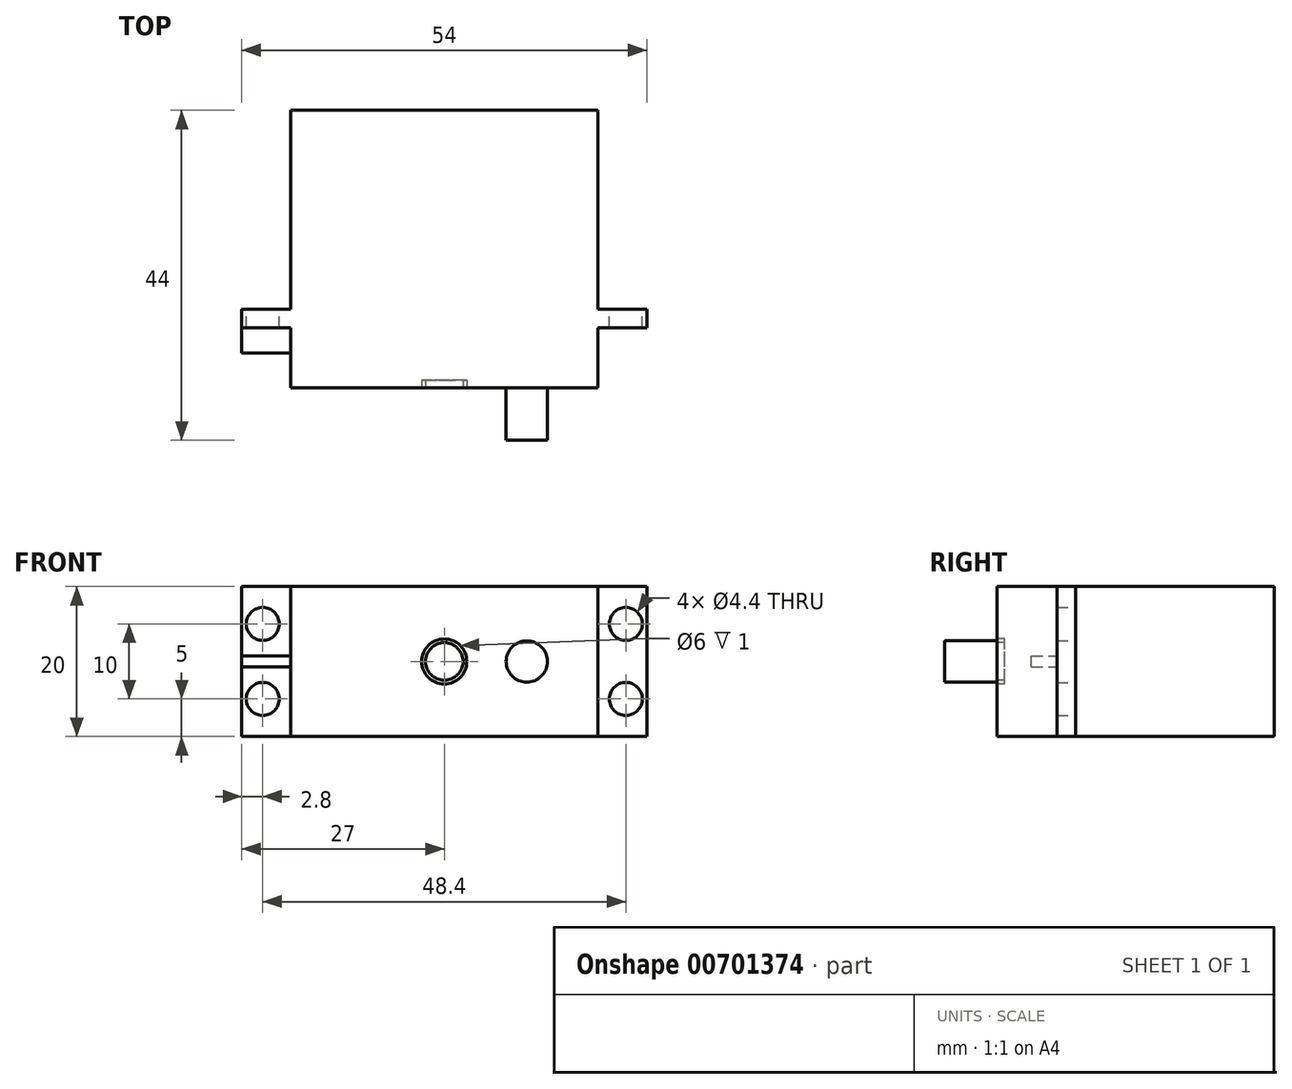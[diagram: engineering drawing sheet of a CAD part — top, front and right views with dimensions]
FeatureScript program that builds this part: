
annotation { "Feature Type Name" : "Feature", "Feature Type Description" : "" }
export const myFeature = defineFeature(function(context is Context, id is Id, definition is map)
    precondition{}
    {
        {
            var Q0;
            Q0=qCreatedBy(makeId("Front.planeOp"),FACE);
            var sketch = newSketch(context, id + "F0", { "sketchPlane" : qUnion([Q0])});
            skLineSegment(sketch, "E0.bottom", {"start": v(20.5, -10) * mm, "end": v(-20.5, -10) * mm});
            skLineSegment(sketch, "E0.top", {"start": v(20.5, 10) * mm, "end": v(-20.5, 10) * mm});
            skLineSegment(sketch, "E0.left", {"start": v(20.5, -10) * mm, "end": v(20.5, 10) * mm});
            skLineSegment(sketch, "E0.right", {"start": v(-20.5, -10) * mm, "end": v(-20.5, 10) * mm});
            skPoint(sketch, "E0.middle", {"position": v(0, 0) * mm});
            skSolve(sketch);
        }
        {
            var Q0;
            Q0=makeQuery(id+"F0.imprint","IMPRINT",FACE,{"disambiguationData":[TD([[makeQuery(id+"F0.imprint","IMPRINT",EDGE,{"derivedFrom":sQuery(id+"F0.wireOp",EDGE,"E0.bottom")}),-1.0]])]});
            extrude(context, id + "F1", {"entities" : qUnion([Q0]), "depth" : 26.5 * mm});
        }
        {
            var Q0;
            Q0=makeQuery(id+"F1.opExtrude","CAP_FACE",FACE,{"disambiguationData":[OSD([sQuery(id+"F0.wireOp",EDGE,"E0.bottom"),sQuery(id+"F0.wireOp",EDGE,"E0.top"),sQuery(id+"F0.wireOp",EDGE,"E0.left"),sQuery(id+"F0.wireOp",EDGE,"E0.right")])],"isStart":false});
            var sketch = newSketch(context, id + "F2", { "sketchPlane" : qUnion([Q0])});
            skLineSegment(sketch, "E1.bottom", {"start": v(27, -10) * mm, "end": v(-27, -10) * mm});
            skLineSegment(sketch, "E1.top", {"start": v(27, 10) * mm, "end": v(-27, 10) * mm});
            skLineSegment(sketch, "E1.left", {"start": v(27, -10) * mm, "end": v(27, 10) * mm});
            skLineSegment(sketch, "E1.right", {"start": v(-27, -10) * mm, "end": v(-27, 10) * mm});
            skPoint(sketch, "E1.middle", {"position": v(0, 0) * mm});
            skCircle(sketch, "E2", {"center": v(24.2, 5) * mm, "radius": 2.2 * mm});
            skCircle(sketch, "E3.MirrorC", {"center": v(24.2, -5) * mm, "radius": 2.2 * mm});
            skCircle(sketch, "E4.MirrorC", {"center": v(-24.2, -5) * mm, "radius": 2.2 * mm});
            skCircle(sketch, "E5.MirrorC", {"center": v(-24.2, 5) * mm, "radius": 2.2 * mm});
            skSolve(sketch);
        }
        {
            var Q0;
            {var subQ0=sQuery(id+"F2.wireOp",EDGE,"E1.right");Q0=makeQuery(id+"F2.imprint","IMPRINT",FACE,{"disambiguationData":[TD([[makeQuery(id+"F2.imprint","IMPRINT",EDGE,{"derivedFrom":subQ0}),-1.0]])]});}
            var Q1;
            {var subQ0=sQuery(id+"F2.wireOp",EDGE,"E1.left");Q1=makeQuery(id+"F2.imprint","IMPRINT",FACE,{"disambiguationData":[TD([[makeQuery(id+"F2.imprint","IMPRINT",EDGE,{"derivedFrom":subQ0}),1.0]])]});}
            var Q2;
            {var subQ1=makeQuery(id+"F1.opExtrude","CAP_EDGE",EDGE,{"disambiguationData":[OSD([sQuery(id+"F0.wireOp",EDGE,"E0.left")])],"isStart":false});Q2=makeQuery(id+"F2.imprint","IMPRINT",FACE,{"disambiguationData":[TD([[makeQuery(id+"F2.imprint","IMPRINT",EDGE,{"derivedFrom":subQ1}),1.0]])]});}
            extrude(context, id + "F3", {"entities" : qUnion([Q0, Q1, Q2]), "operationType" : NewBodyOperationType.ADD, "depth" : 2.5 * mm});
        }
        {
            var Q0;
            Q0=makeQuery(id+"F3.opExtrude","CAP_FACE",FACE,{"disambiguationData":[OSD([sQuery(id+"F2.wireOp",EDGE,"E1.bottom"),sQuery(id+"F2.wireOp",EDGE,"E1.top"),sQuery(id+"F2.wireOp",EDGE,"E1.left"),sQuery(id+"F2.wireOp",EDGE,"E1.right"),sQuery(id+"F2.wireOp",EDGE,"E2"),sQuery(id+"F2.wireOp",EDGE,"E3.MirrorC"),sQuery(id+"F2.wireOp",EDGE,"E4.MirrorC"),sQuery(id+"F2.wireOp",EDGE,"E5.MirrorC")])],"isStart":false});
            var sketch = newSketch(context, id + "F4", { "sketchPlane" : qUnion([Q0])});
            skLineSegment(sketch, "E6.bottom", {"start": v(20.5, -10) * mm, "end": v(-20.5, -10) * mm});
            skLineSegment(sketch, "E6.top", {"start": v(20.5, 10) * mm, "end": v(-20.5, 10) * mm});
            skLineSegment(sketch, "E6.left", {"start": v(20.5, -10) * mm, "end": v(20.5, 10) * mm});
            skLineSegment(sketch, "E6.right", {"start": v(-20.5, -10) * mm, "end": v(-20.5, 10) * mm});
            skPoint(sketch, "E6.middle", {"position": v(0, 0) * mm});
            skSolve(sketch);
        }
        {
            var Q0;
            Q0=makeQuery(id+"F4.imprint","IMPRINT",FACE,{"disambiguationData":[TD([[makeQuery(id+"F4.imprint","IMPRINT",EDGE,{"derivedFrom":sQuery(id+"F4.wireOp",EDGE,"E6.bottom")}),-1.0]])]});
            extrude(context, id + "F5", {"entities" : qUnion([Q0]), "operationType" : NewBodyOperationType.ADD, "depth" : 8 * mm});
        }
        {
            var Q0;
            {var subQ0=sQuery(id+"F2.wireOp",EDGE,"E5.MirrorC");var subQ1=sQuery(id+"F2.wireOp",EDGE,"E1.top");var subQ2=sQuery(id+"F2.wireOp",EDGE,"E1.bottom");var subQ3=sQuery(id+"F2.wireOp",EDGE,"E1.right");var subQ4=sQuery(id+"F2.wireOp",EDGE,"E4.MirrorC");Q0=makeQuery(id+"F5.boolean.opBoolean","SPLIT",FACE,{"disambiguationData":[TD([makeQuery(id+"F3.opExtrude","SWEPT_FACE",FACE,{"disambiguationData":[OSD([subQ3])]})])],"derivedFrom":makeQuery(id+"F3.opExtrude","CAP_FACE",FACE,{"disambiguationData":[OSD([subQ2,subQ1,sQuery(id+"F2.wireOp",EDGE,"E1.left"),subQ3,sQuery(id+"F2.wireOp",EDGE,"E2"),sQuery(id+"F2.wireOp",EDGE,"E3.MirrorC"),subQ4,subQ0])],"isStart":false})});}
            var sketch = newSketch(context, id + "F6", { "sketchPlane" : qUnion([Q0])});
            skLineSegment(sketch, "E7.bottom", {"start": v(-20.5, 0.75) * mm, "end": v(-27, 0.75) * mm});
            skLineSegment(sketch, "E7.top", {"start": v(-20.5, -0.75) * mm, "end": v(-27, -0.75) * mm});
            skLineSegment(sketch, "E7.left", {"start": v(-20.5, 0.75) * mm, "end": v(-20.5, -0.75) * mm});
            skLineSegment(sketch, "E7.right", {"start": v(-27, 0.75) * mm, "end": v(-27, -0.75) * mm});
            skPoint(sketch, "E7.middle", {"position": v(-23.75, 0) * mm});
            skSolve(sketch);
        }
        {
            var Q0;
            Q0=makeQuery(id+"F6.imprint","IMPRINT",FACE,{"disambiguationData":[TD([[makeQuery(id+"F6.imprint","IMPRINT",EDGE,{"derivedFrom":sQuery(id+"F6.wireOp",EDGE,"E7.bottom")}),1.0]])]});
            var Q1;
            Q1=makeQuery(id+"F5.opExtrude","CAP_FACE",FACE,{"disambiguationData":[OSD([sQuery(id+"F4.wireOp",EDGE,"E6.bottom"),sQuery(id+"F4.wireOp",EDGE,"E6.top"),sQuery(id+"F4.wireOp",EDGE,"E6.left"),sQuery(id+"F4.wireOp",EDGE,"E6.right")])],"isStart":false});
            extrude(context, id + "F7", {"entities" : qUnion([Q0]), "operationType" : NewBodyOperationType.ADD, "endBoundEntityFace" : qUnion([Q1]), "depth" : 3.4 * mm});
        }
        {
            var Q0;
            Q0=makeQuery(id+"F5.opExtrude","CAP_FACE",FACE,{"disambiguationData":[OSD([sQuery(id+"F4.wireOp",EDGE,"E6.bottom"),sQuery(id+"F4.wireOp",EDGE,"E6.top"),sQuery(id+"F4.wireOp",EDGE,"E6.left"),sQuery(id+"F4.wireOp",EDGE,"E6.right")])],"isStart":false});
            var sketch = newSketch(context, id + "F8", { "sketchPlane" : qUnion([Q0])});
            skCircle(sketch, "E8", {"center": v(11, 0) * mm, "radius": 2.75 * mm});
            skSolve(sketch);
        }
        {
            var Q0;
            Q0=makeQuery(id+"F8.imprint","IMPRINT",FACE,{"disambiguationData":[TD([[makeQuery(id+"F8.imprint","IMPRINT",EDGE,{"derivedFrom":sQuery(id+"F8.wireOp",EDGE,"E8")}),1.0]])]});
            extrude(context, id + "F9", {"entities" : qUnion([Q0]), "operationType" : NewBodyOperationType.ADD, "depth" : 7 * mm});
        }
        {
            var Q0;
            Q0=makeQuery(id+"F5.opExtrude","CAP_FACE",FACE,{"disambiguationData":[OSD([sQuery(id+"F4.wireOp",EDGE,"E6.bottom"),sQuery(id+"F4.wireOp",EDGE,"E6.top"),sQuery(id+"F4.wireOp",EDGE,"E6.left"),sQuery(id+"F4.wireOp",EDGE,"E6.right")])],"isStart":false});
            var sketch = newSketch(context, id + "F10", { "sketchPlane" : qUnion([Q0])});
            skCircle(sketch, "E9", {"center": v(0, 0) * mm, "radius": 2.5 * mm});
            skCircle(sketch, "E10", {"center": v(0, 0) * mm, "radius": 3 * mm});
            skSolve(sketch);
        }
        {
            var Q0;
            Q0=makeQuery(id+"F10.imprint","IMPRINT",FACE,{"disambiguationData":[TD([[makeQuery(id+"F10.imprint","IMPRINT",EDGE,{"derivedFrom":sQuery(id+"F10.wireOp",EDGE,"E9")}),-1.0]])]});
            extrude(context, id + "F11", {"entities" : qUnion([Q0]), "operationType" : NewBodyOperationType.REMOVE, "oppositeDirection" : true, "depth" : 1 * mm});
        }
    });
